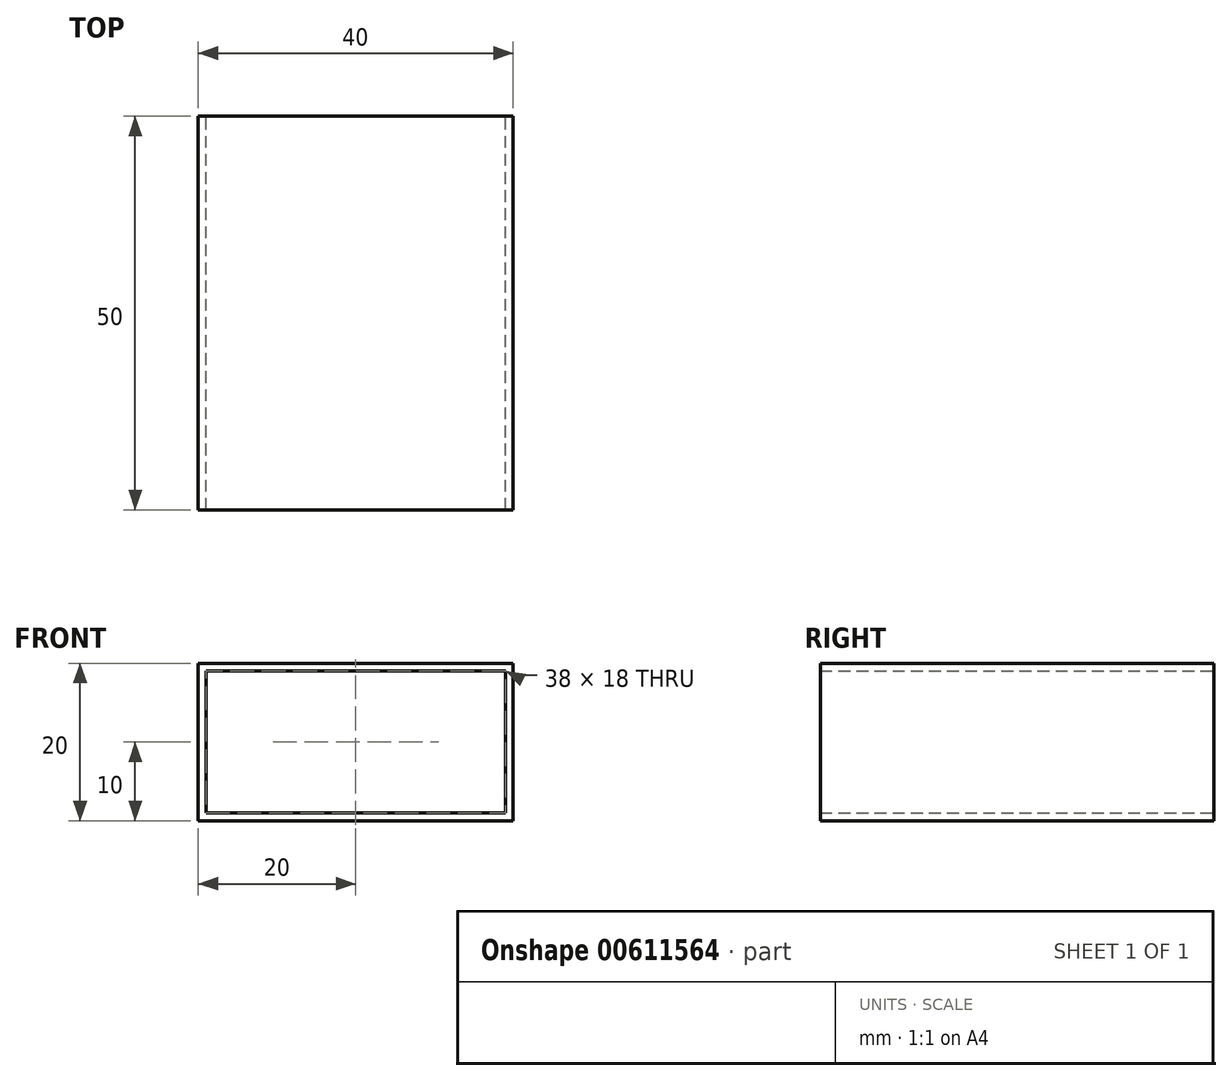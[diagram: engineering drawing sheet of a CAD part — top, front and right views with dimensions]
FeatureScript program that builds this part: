
annotation { "Feature Type Name" : "Feature", "Feature Type Description" : "" }
export const myFeature = defineFeature(function(context is Context, id is Id, definition is map)
    precondition{}
    {
        {
            var Q0;
            Q0=qCreatedBy(makeId("Front.planeOp"),FACE);
            var sketch = newSketch(context, id + "F0", { "sketchPlane" : qUnion([Q0])});
            skLineSegment(sketch, "E0.bottom", {"start": v(-20, -10) * mm, "end": v(20, -10) * mm});
            skLineSegment(sketch, "E0.top", {"start": v(-20, 10) * mm, "end": v(20, 10) * mm});
            skLineSegment(sketch, "E0.left", {"start": v(-20, -10) * mm, "end": v(-20, 10) * mm});
            skLineSegment(sketch, "E0.right", {"start": v(20, -10) * mm, "end": v(20, 10) * mm});
            skPoint(sketch, "E0.middle", {"position": v(0, 0) * mm});
            skLineSegment(sketch, "E1", {"start": v(-20, 10) * mm, "end": v(-19, 10) * mm});
            skLineSegment(sketch, "E2", {"start": v(-19, 10) * mm, "end": v(-19, -10) * mm});
            skLineSegment(sketch, "E3", {"start": v(-19, -10) * mm, "end": v(-19, -9) * mm});
            skLineSegment(sketch, "E4", {"start": v(-19, -9) * mm, "end": v(20, -9) * mm});
            skLineSegment(sketch, "E5.MirrorCS", {"start": v(19, 10) * mm, "end": v(19, -10) * mm});
            skLineSegment(sketch, "E6.MirrorCS", {"start": v(-19, 9) * mm, "end": v(20, 9) * mm});
            skSolve(sketch);
        }
        {
            var Q0;
            Q0 = qSketchRegion(id + "F0", true);
            extrude(context, id + "F1", {"entities" : qUnion([Q0]), "depth" : 50 * mm, "offsetDistance" : 25 * mm});
        }
    });
